# Revit family: Faucet-Wall_Mount-ITB-KOHLER-Constellation_Composed-K-181025_1
name_source: partatom
category: Plumbing Fixtures
units: mm (PartAtom-declared; Revit-internal decimal feet)

## family parameters
Cut with Voids When Loaded = No
Host = Face
OmniClass Number = 23.31.11.00
OmniClass Title = Faucets
Part Type = Normal
Room Calculation Point = No
Round Connector Dimension = Use Diameter
Shared = No

## types (4) — shared parameters
ADA Compliant = No
Apparent Load = 72 VA
Assembly Code = D2010
CW Connection = Yes
Cold Water Inlet 1 = Cold Water Inlet 1
Cold Water Inlet 2 = Cold Water Inlet 2
Date Modified = 04/24/2023
Default Elevation = 36"
Description = 60inch Basin Wall Mount
Drain Included = Yes
Electrical Connector = Yes
Electrical Note = One Dedicated Circuit Required
Flow Rate = 1 GPM
HW Connection = Yes
Height = 26 13/16"
Hot Water Inlet 1 = Hot Water Inlet 1
Hot Water Inlet 2 = Hot Water Inlet 2
Length = 24 5/16"
Manufacturer = Kohler Co.
Master Format 2014 = 22 41 39
Master Format 2014 Name = Residential Faucets, Supplies, and Trim
Material = Premium Metal Construction
Pressure = 60.00 psi
Product Documentation Link = https://www.us.kohler.com
Product Name = Constellation Composed
Product Page URL = http://www.us.kohler.com
Spout Reach = 6 7/16"
URL = https://www.us.kohler.com
Vent Connection = No
Voltage = 240 V
Waste Connection = Yes
Waste Water Outlet 1 = Waste Water Outlet 1
Waste Water Outlet 2 = Waste Water Outlet 2
WaterSense Certified = No
Width = 55 1/8"

## per-type parameters (varying)
| type | Finish | Model | Type |
| CP-Polished Chrome | Kohler-Metal-CP-Polished_Chrome | K-181025-BC1-CP | 1 |
| BN-Vibrant Brushed Nickel | Kohler-Metal-BN-Vibrant_Brushed_Nickel | K-181025-BC1-BN | 2 |
| BL-Matte Black | Kohler-Metal-BL-Matte_Black | K-181025-BC1-BL | 3 |
| 2MB-Vibrant Brushed Moderne Brass | Kohler-Metal-2MB-Vibrant_Brushed_Moderne_Brass | K-181025-BC1-2MB | 4 |

## geometry (parser evidence)
native form markers: Sweep x22
no freeform markers — native parametric forms only
